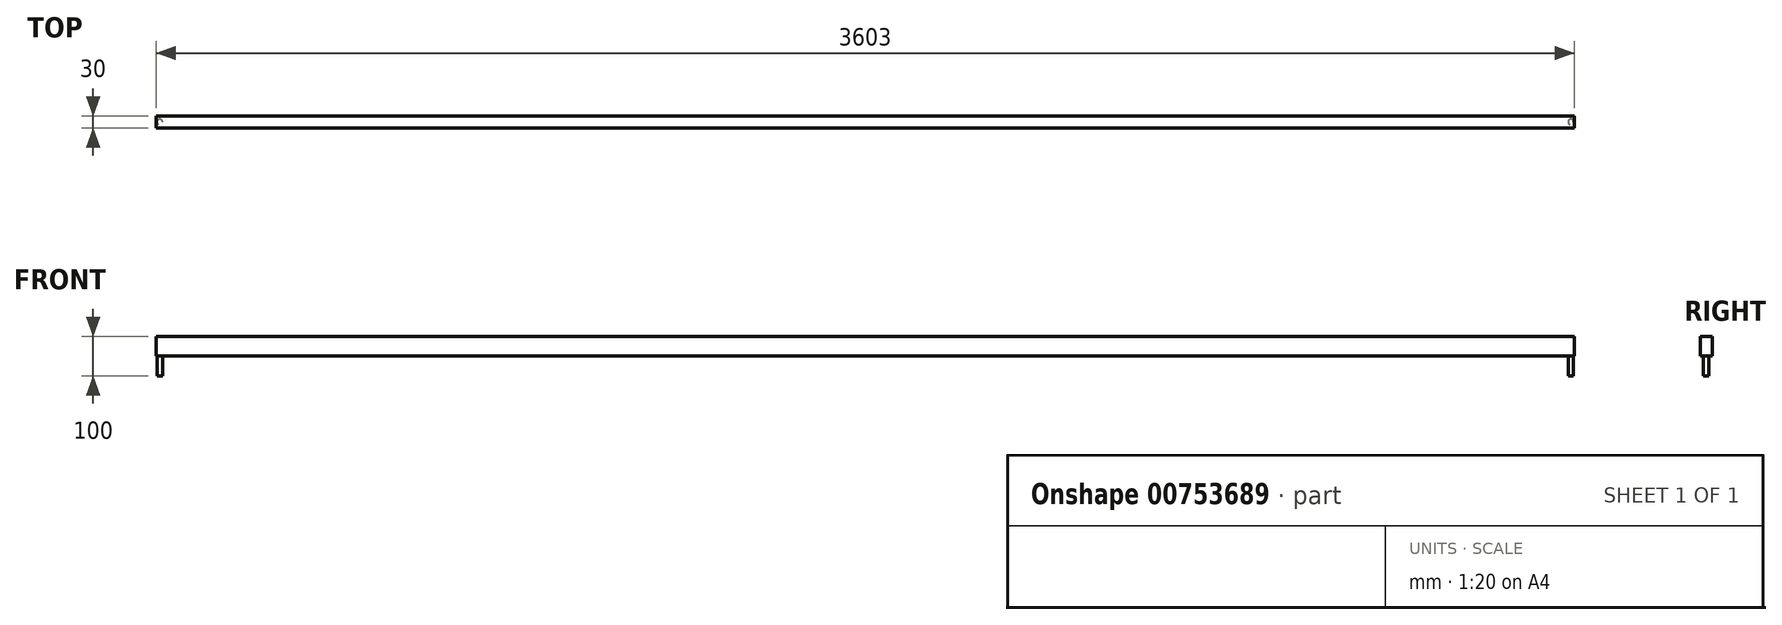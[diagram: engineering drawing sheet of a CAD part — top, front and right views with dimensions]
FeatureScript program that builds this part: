
annotation { "Feature Type Name" : "Feature", "Feature Type Description" : "" }
export const myFeature = defineFeature(function(context is Context, id is Id, definition is map)
    precondition{}
    {
        {
            var Q0;
            Q0=qCreatedBy(makeId("Front.planeOp"),FACE);
            var sketch = newSketch(context, id + "F0", { "sketchPlane" : qUnion([Q0])});
            skLineSegment(sketch, "E0.bottom", {"start": v(1801.5, -25) * mm, "end": v(-1801.5, -25) * mm});
            skLineSegment(sketch, "E0.top", {"start": v(1801.5, 25) * mm, "end": v(-1801.5, 25) * mm});
            skLineSegment(sketch, "E0.left", {"start": v(1801.5, -25) * mm, "end": v(1801.5, 25) * mm});
            skLineSegment(sketch, "E0.right", {"start": v(-1801.5, -25) * mm, "end": v(-1801.5, 25) * mm});
            skPoint(sketch, "E0.middle", {"position": v(0, 0) * mm});
            skSolve(sketch);
        }
        {
            var Q0;
            Q0=qSketchRegion(id+"F0",true);
            extrude(context, id + "F1", {"entities" : qUnion([Q0]), "depth" : 15 * mm, "offsetDistance" : 25 * mm, "hasSecondDirection" : true, "secondDirectionOppositeDirection" : true, "secondDirectionDepth" : 15 * mm});
        }
        {
            var Q0;
            Q0=makeQuery(id+"F1.opExtrude","SWEPT_FACE",FACE,{"disambiguationData":[OSD([sQuery(id+"F0.wireOp",EDGE,"E0.bottom")])]});
            var sketch = newSketch(context, id + "F2", { "sketchPlane" : qUnion([Q0])});
            skLineSegment(sketch, "E1.0", {"start": v(-1801.5, 15) * mm, "end": v(-1801.5, -15) * mm});
            skLineSegment(sketch, "E2", {"start": v(-1801.5, 0) * mm, "end": v(-1799.5, 0) * mm});
            skLineSegment(sketch, "E3", {"start": v(-1799.5, 0) * mm, "end": v(-1792.5, 0) * mm});
            skCircle(sketch, "E4", {"center": v(-1792.5, 0) * mm, "radius": 7 * mm});
            skSolve(sketch);
        }
        {
            var Q0;
            Q0=qSketchRegion(id+"F2",true);
            extrude(context, id + "F3", {"entities" : qUnion([Q0]), "operationType" : NewBodyOperationType.ADD, "depth" : 50 * mm, "offsetDistance" : 25 * mm});
        }
        {
            var Q0;
            Q0=makeQuery(id+"F1.opExtrude","SWEPT_FACE",FACE,{"disambiguationData":[OSD([sQuery(id+"F0.wireOp",EDGE,"E0.bottom")])]});
            var sketch = newSketch(context, id + "F4", { "sketchPlane" : qUnion([Q0])});
            skLineSegment(sketch, "E5.0", {"start": v(1801.5, 15) * mm, "end": v(1801.5, -15) * mm});
            skLineSegment(sketch, "E6", {"start": v(1801.5, 0) * mm, "end": v(1799.5, 0) * mm});
            skLineSegment(sketch, "E7", {"start": v(1799.5, 0) * mm, "end": v(1792.5, 0) * mm});
            skCircle(sketch, "E8", {"center": v(1792.5, 0) * mm, "radius": 7 * mm});
            skSolve(sketch);
        }
        {
            var Q0;
            Q0=qSketchRegion(id+"F4",true);
            extrude(context, id + "F5", {"entities" : qUnion([Q0]), "operationType" : NewBodyOperationType.ADD, "depth" : 50 * mm, "offsetDistance" : 25 * mm});
        }
    });
